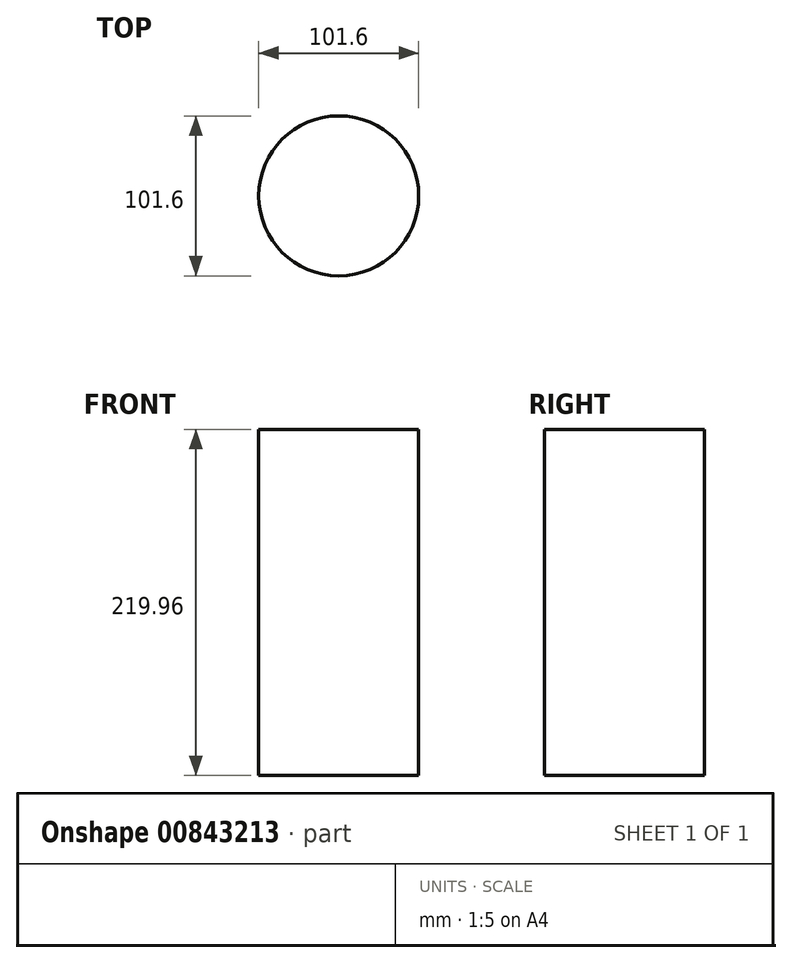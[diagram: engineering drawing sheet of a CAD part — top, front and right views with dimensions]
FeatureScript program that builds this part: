
annotation { "Feature Type Name" : "Feature", "Feature Type Description" : "" }
export const myFeature = defineFeature(function(context is Context, id is Id, definition is map)
    precondition{}
    {
        {
            var Q0;
            Q0=qCreatedBy(makeId("Top.planeOp"),FACE);
            var sketch = newSketch(context, id + "F0", { "sketchPlane" : qUnion([Q0])});
            skCircle(sketch, "E0", {"center": v(0, 0) * mm, "radius": 50.8 * mm});
            skSolve(sketch);
        }
        {
            var Q0;
            Q0=makeQuery(id+"F0.imprint","IMPRINT",FACE,{"disambiguationData":[TD([[makeQuery(id+"F0.imprint","IMPRINT",EDGE,{"derivedFrom":sQuery(id+"F0.wireOp",EDGE,"E0")}),1.0]])]});
            extrude(context, id + "F1", {"entities" : qUnion([Q0]), "endBound" : BoundingType.SYMMETRIC, "depth" : 219.96 * mm, "offsetDistance" : 25.4 * mm});
        }
    });
